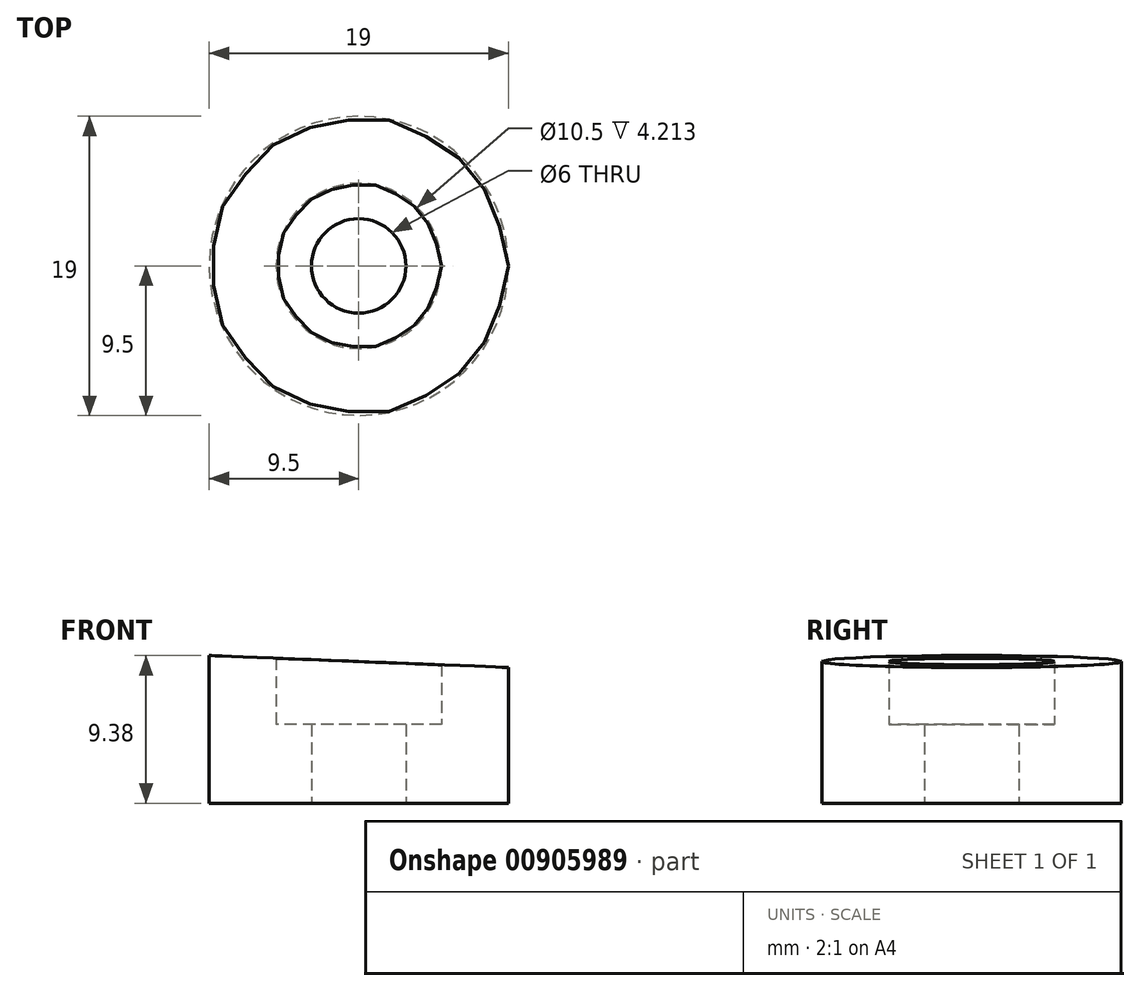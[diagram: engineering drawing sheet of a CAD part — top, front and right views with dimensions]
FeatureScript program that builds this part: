
annotation { "Feature Type Name" : "Feature", "Feature Type Description" : "" }
export const myFeature = defineFeature(function(context is Context, id is Id, definition is map)
    precondition{}
    {
        {
            var Q0;
            Q0=qCreatedBy(makeId("Top.planeOp"),FACE);
            var sketch = newSketch(context, id + "F0", { "sketchPlane" : qUnion([Q0])});
            skCircle(sketch, "E0", {"center": v(0, 0) * mm, "radius": 5.25 * mm});
            skCircle(sketch, "E1", {"center": v(0, 0) * mm, "radius": 9.5 * mm});
            skSolve(sketch);
        }
        {
            var Q0;
            Q0=qSketchRegion(id+"F0",true);
            extrude(context, id + "F1", {"entities" : qUnion([Q0]), "depth" : 10 * mm, "offsetDistance" : 25 * mm});
        }
        {
            var Q0;
            Q0=qCreatedBy(makeId("Top.planeOp"),FACE);
            var sketch = newSketch(context, id + "F2", { "sketchPlane" : qUnion([Q0])});
            skCircle(sketch, "E2", {"center": v(0, 0) * mm, "radius": 3 * mm});
            skCircle(sketch, "E3.0", {"center": v(0, 0) * mm, "radius": 5.25 * mm});
            skSolve(sketch);
        }
        {
            var Q0;
            Q0=qSketchRegion(id+"F2",true);
            extrude(context, id + "F3", {"entities" : qUnion([Q0]), "operationType" : NewBodyOperationType.ADD, "depth" : 5 * mm, "offsetDistance" : 25 * mm});
        }
        {
            var Q0;
            Q0=qCreatedBy(makeId("Front.planeOp"),FACE);
            var sketch = newSketch(context, id + "F4", { "sketchPlane" : qUnion([Q0])});
            skLineSegment(sketch, "E4.bottom", {"start": v(-25, 10) * mm, "end": v(25, 8) * mm});
            skLineSegment(sketch, "E4.top", {"start": v(-25, 0) * mm, "end": v(25, 0) * mm});
            skLineSegment(sketch, "E4.left", {"start": v(-25, 10) * mm, "end": v(-25, 0) * mm});
            skLineSegment(sketch, "E4.right", {"start": v(25, 8) * mm, "end": v(25, 0) * mm});
            skPoint(sketch, "E5", {"position": v(0, 9) * mm});
            skLineSegment(sketch, "E6.0", {"start": v(-9.5, 10) * mm, "end": v(9.5, 10) * mm});
            skSolve(sketch);
        }
        {
            var Q0;
            Q0=qSketchRegion(id+"F4",true);
            extrude(context, id + "F5", {"entities" : qUnion([Q0]), "operationType" : NewBodyOperationType.INTERSECT, "endBound" : BoundingType.SYMMETRIC, "oppositeDirection" : true, "depth" : 25 * mm, "offsetDistance" : 25 * mm});
        }
    });
